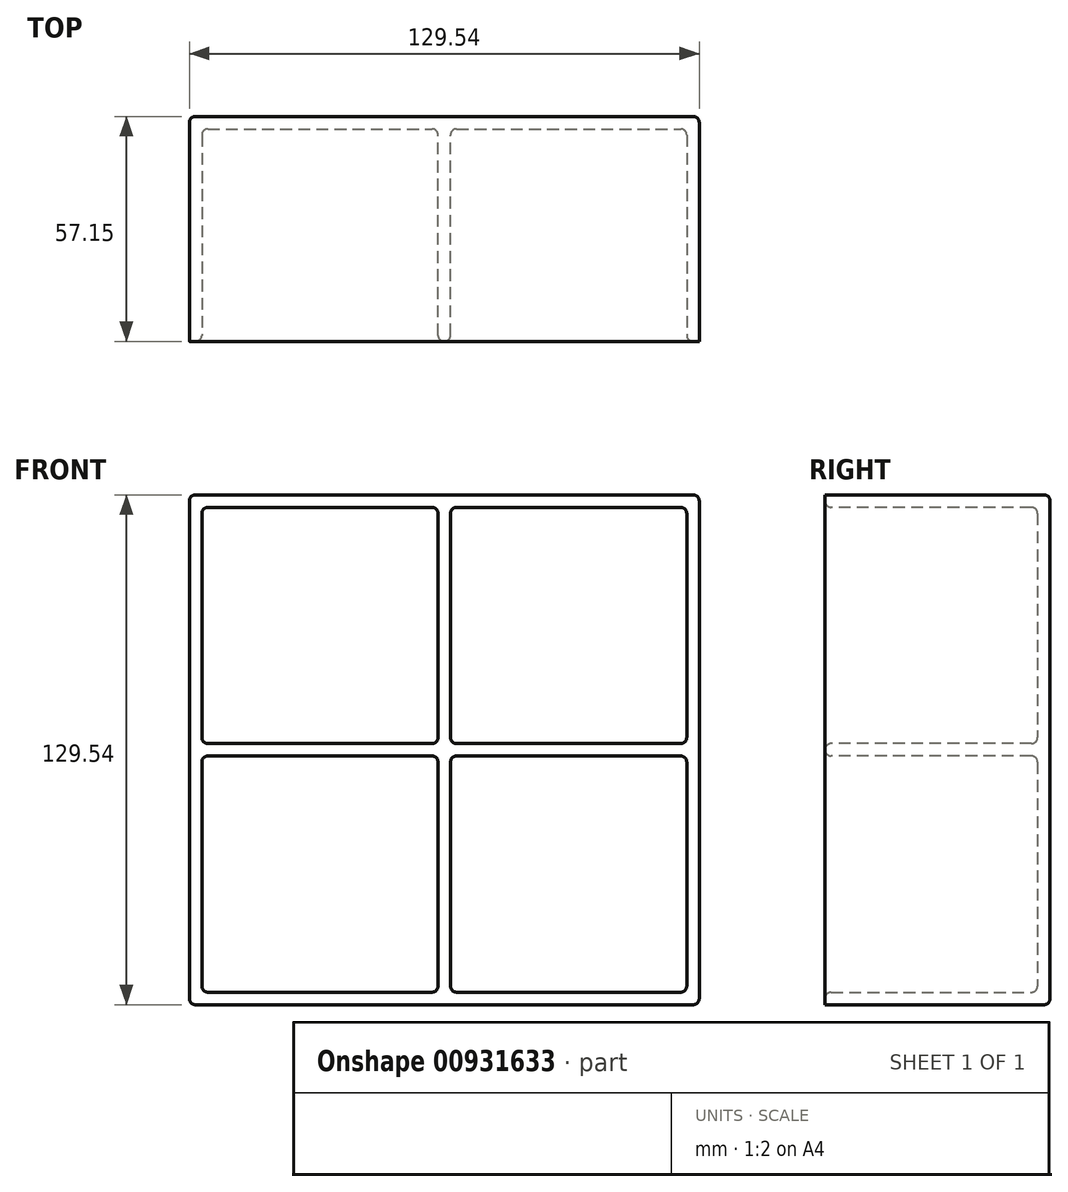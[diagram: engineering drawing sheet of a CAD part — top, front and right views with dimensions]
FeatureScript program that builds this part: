
annotation { "Feature Type Name" : "Feature", "Feature Type Description" : "" }
export const myFeature = defineFeature(function(context is Context, id is Id, definition is map)
    precondition{}
    {
        {
            var Q0;
            Q0=qCreatedBy(makeId("Front.planeOp"),FACE);
            var sketch = newSketch(context, id + "F0", { "sketchPlane" : qUnion([Q0])});
            skLineSegment(sketch, "E0.bottom", {"start": v(0, 0) * mm, "end": v(129.54, 0) * mm});
            skLineSegment(sketch, "E0.top", {"start": v(0, 129.54) * mm, "end": v(129.54, 129.54) * mm});
            skLineSegment(sketch, "E0.left", {"start": v(0, 0) * mm, "end": v(0, 129.54) * mm});
            skLineSegment(sketch, "E0.right", {"start": v(129.54, 0) * mm, "end": v(129.54, 129.54) * mm});
            skSolve(sketch);
        }
        {
            var Q0;
            Q0=makeQuery(id+"F0.imprint","IMPRINT",FACE,{"disambiguationData":[TD([[makeQuery(id+"F0.imprint","IMPRINT",EDGE,{"derivedFrom":sQuery(id+"F0.wireOp",EDGE,"E0.bottom")}),1.0]])]});
            extrude(context, id + "F1", {"entities" : qUnion([Q0]), "oppositeDirection" : true, "depth" : 57.15 * mm, "offsetDistance" : 25.4 * mm});
        }
        {
            var Q0;
            Q0=makeQuery(id+"F1.opExtrude","CAP_FACE",FACE,{"disambiguationData":[OSD([sQuery(id+"F0.wireOp",EDGE,"E0.bottom"),sQuery(id+"F0.wireOp",EDGE,"E0.top"),sQuery(id+"F0.wireOp",EDGE,"E0.left"),sQuery(id+"F0.wireOp",EDGE,"E0.right")])],"isStart":true});
            shell(context, id + "F2", {"entities" : qUnion([Q0]), "thickness" : 3.17 * mm});
        }
        {
            var Q0;
            Q0=makeQuery(id+"F2.opShell","OFFSET_EDGE",EDGE,{"disambiguationData":[OSD([sQuery(id+"F0.wireOp",EDGE,"E0.top"),sQuery(id+"F0.wireOp",EDGE,"E0.left")])]});
            var Q1;
            {var subQ0=sQuery(id+"F0.wireOp",EDGE,"E0.top");Q1=makeQuery(id+"F2.opShell","OFFSET_EDGE",EDGE,{"disambiguationData":[OSD([subQ0]),TDD([makeQuery(id+"F1.opExtrude","CAP_EDGE",EDGE,{"disambiguationData":[OSD([subQ0])],"isStart":false})])]});}
            var Q2;
            {var subQ0=sQuery(id+"F0.wireOp",EDGE,"E0.left");Q2=makeQuery(id+"F2.opShell","OFFSET_EDGE",EDGE,{"disambiguationData":[OSD([subQ0]),TDD([makeQuery(id+"F1.opExtrude","CAP_EDGE",EDGE,{"disambiguationData":[OSD([subQ0])],"isStart":false})])]});}
            var Q3;
            Q3=makeQuery(id+"F2.opShell","OFFSET_EDGE",EDGE,{"disambiguationData":[OSD([sQuery(id+"F0.wireOp",EDGE,"E0.bottom"),sQuery(id+"F0.wireOp",EDGE,"E0.left")])]});
            var Q4;
            {var subQ0=sQuery(id+"F0.wireOp",EDGE,"E0.bottom");Q4=makeQuery(id+"F2.opShell","OFFSET_EDGE",EDGE,{"disambiguationData":[OSD([subQ0]),TDD([makeQuery(id+"F1.opExtrude","CAP_EDGE",EDGE,{"disambiguationData":[OSD([subQ0])],"isStart":false})])]});}
            var Q5;
            {var subQ0=sQuery(id+"F0.wireOp",EDGE,"E0.right");Q5=makeQuery(id+"F2.opShell","OFFSET_EDGE",EDGE,{"disambiguationData":[OSD([subQ0]),TDD([makeQuery(id+"F1.opExtrude","CAP_EDGE",EDGE,{"disambiguationData":[OSD([subQ0])],"isStart":false})])]});}
            var Q6;
            Q6=makeQuery(id+"F2.opShell","OFFSET_EDGE",EDGE,{"disambiguationData":[OSD([sQuery(id+"F0.wireOp",EDGE,"E0.top"),sQuery(id+"F0.wireOp",EDGE,"E0.right")])]});
            var Q7;
            Q7=makeQuery(id+"F2.opShell","OFFSET_EDGE",EDGE,{"disambiguationData":[OSD([sQuery(id+"F0.wireOp",EDGE,"E0.bottom"),sQuery(id+"F0.wireOp",EDGE,"E0.right")])]});
            fillet(context, id + "F3", {"entities" : qUnion([Q0, Q1, Q2, Q3, Q4, Q5, Q6, Q7]), "radius" : 1.52 * mm, "tangentPropagation" : true, "allowEdgeOverflow" : false});
        }
        {
            var Q0;
            Q0=makeQuery(id+"F1.opExtrude","SWEPT_EDGE",EDGE,{"disambiguationData":[OSD([sQuery(id+"F0.wireOp",EDGE,"E0.bottom"),sQuery(id+"F0.wireOp",EDGE,"E0.right")])]});
            var Q1;
            Q1=makeQuery(id+"F1.opExtrude","CAP_EDGE",EDGE,{"disambiguationData":[OSD([sQuery(id+"F0.wireOp",EDGE,"E0.bottom")])],"isStart":false});
            var Q2;
            Q2=makeQuery(id+"F1.opExtrude","CAP_EDGE",EDGE,{"disambiguationData":[OSD([sQuery(id+"F0.wireOp",EDGE,"E0.right")])],"isStart":false});
            var Q3;
            Q3=makeQuery(id+"F1.opExtrude","SWEPT_EDGE",EDGE,{"disambiguationData":[OSD([sQuery(id+"F0.wireOp",EDGE,"E0.top"),sQuery(id+"F0.wireOp",EDGE,"E0.right")])]});
            var Q4;
            Q4=makeQuery(id+"F1.opExtrude","CAP_EDGE",EDGE,{"disambiguationData":[OSD([sQuery(id+"F0.wireOp",EDGE,"E0.top")])],"isStart":false});
            var Q5;
            Q5=makeQuery(id+"F1.opExtrude","SWEPT_EDGE",EDGE,{"disambiguationData":[OSD([sQuery(id+"F0.wireOp",EDGE,"E0.top"),sQuery(id+"F0.wireOp",EDGE,"E0.left")])]});
            var Q6;
            Q6=makeQuery(id+"F1.opExtrude","CAP_EDGE",EDGE,{"disambiguationData":[OSD([sQuery(id+"F0.wireOp",EDGE,"E0.left")])],"isStart":false});
            var Q7;
            Q7=makeQuery(id+"F1.opExtrude","SWEPT_EDGE",EDGE,{"disambiguationData":[OSD([sQuery(id+"F0.wireOp",EDGE,"E0.bottom"),sQuery(id+"F0.wireOp",EDGE,"E0.left")])]});
            fillet(context, id + "F4", {"entities" : qUnion([Q0, Q1, Q2, Q3, Q4, Q5, Q6, Q7]), "radius" : 1.52 * mm, "tangentPropagation" : true, "allowEdgeOverflow" : false});
        }
        {
            var Q0;
            Q0=makeQuery(id+"F2.opShell","OFFSET_FACE",FACE,{"disambiguationData":[OSD([sQuery(id+"F0.wireOp",EDGE,"E0.bottom"),sQuery(id+"F0.wireOp",EDGE,"E0.top"),sQuery(id+"F0.wireOp",EDGE,"E0.left"),sQuery(id+"F0.wireOp",EDGE,"E0.right")])]});
            var sketch = newSketch(context, id + "F5", { "sketchPlane" : qUnion([Q0])});
            skLineSegment(sketch, "E1.0", {"start": v(63.18, 126.37) * mm, "end": v(63.18, 3.17) * mm});
            skLineSegment(sketch, "E2.0", {"start": v(66.36, 126.37) * mm, "end": v(66.36, 3.17) * mm});
            skPoint(sketch, "E3.end.orphan", {"position": v(64.77, 3.17) * mm});
            skPoint(sketch, "E3.start.orphan", {"position": v(64.77, 126.37) * mm});
            skLineSegment(sketch, "E4", {"start": v(63.18, 126.37) * mm, "end": v(66.36, 126.37) * mm});
            skLineSegment(sketch, "E5", {"start": v(66.36, 3.17) * mm, "end": v(63.18, 3.17) * mm});
            skSolve(sketch);
        }
        {
            var Q0;
            Q0=makeQuery(id+"F5.imprint","IMPRINT",FACE,{"disambiguationData":[TD([[makeQuery(id+"F5.imprint","IMPRINT",EDGE,{"derivedFrom":sQuery(id+"F5.wireOp",EDGE,"E1.0")}),1.0]])]});
            extrude(context, id + "F6", {"entities" : qUnion([Q0]), "operationType" : NewBodyOperationType.ADD, "depth" : 53.97 * mm, "offsetDistance" : 25.4 * mm});
        }
        {
            var Q0;
            Q0=makeQuery(id+"F6.boolean.opBoolean","MERGE",FACE,{"derivedFrom":[makeQuery(id+"F1.opExtrude","CAP_FACE",FACE,{"disambiguationData":[OSD([sQuery(id+"F0.wireOp",EDGE,"E0.bottom"),sQuery(id+"F0.wireOp",EDGE,"E0.top"),sQuery(id+"F0.wireOp",EDGE,"E0.left"),sQuery(id+"F0.wireOp",EDGE,"E0.right")])],"isStart":true}),makeQuery(id+"F6.opExtrude","CAP_FACE",FACE,{"disambiguationData":[OSD([sQuery(id+"F5.wireOp",EDGE,"E1.0"),sQuery(id+"F5.wireOp",EDGE,"E2.0"),sQuery(id+"F5.wireOp",EDGE,"E4"),sQuery(id+"F5.wireOp",EDGE,"E5")])],"isStart":false})]});
            var sketch = newSketch(context, id + "F7", { "sketchPlane" : qUnion([Q0])});
            skLineSegment(sketch, "E6.0", {"start": v(3.17, 63.18) * mm, "end": v(126.37, 63.18) * mm});
            skLineSegment(sketch, "E7.0", {"start": v(3.17, 66.36) * mm, "end": v(126.37, 66.36) * mm});
            skPoint(sketch, "E8.end.orphan", {"position": v(126.37, 64.77) * mm});
            skPoint(sketch, "E8.start.orphan", {"position": v(3.17, 64.77) * mm});
            skLineSegment(sketch, "E9", {"start": v(3.17, 66.36) * mm, "end": v(3.17, 63.18) * mm});
            skLineSegment(sketch, "E10", {"start": v(126.37, 66.36) * mm, "end": v(126.37, 63.18) * mm});
            skSolve(sketch);
        }
        {
            var Q0;
            {var subQ0=sQuery(id+"F7.wireOp",EDGE,"E10");Q0=makeQuery(id+"F7.imprint","IMPRINT",FACE,{"disambiguationData":[TD([[makeQuery(id+"F7.imprint","IMPRINT",EDGE,{"derivedFrom":subQ0}),1.0]])]});}
            var Q1;
            {var subQ0=sQuery(id+"F7.wireOp",EDGE,"E9");Q1=makeQuery(id+"F7.imprint","IMPRINT",FACE,{"disambiguationData":[TD([[makeQuery(id+"F7.imprint","IMPRINT",EDGE,{"derivedFrom":subQ0}),-1.0]])]});}
            extrude(context, id + "F8", {"entities" : qUnion([Q0, Q1]), "operationType" : NewBodyOperationType.ADD, "oppositeDirection" : true, "depth" : 53.97 * mm, "offsetDistance" : 25.4 * mm});
        }
        {
            var Q0;
            {var subQ0=sQuery(id+"F0.wireOp",EDGE,"E0.top");var subQ4=sQuery(id+"F5.wireOp",EDGE,"E2.0");Q0=makeQuery(id+"F8.boolean.opBoolean","SPLIT",FACE,{"disambiguationData":[TD([makeQuery(id+"F2.opShell","OFFSET_FACE",FACE,{"disambiguationData":[OSD([subQ0])]})])],"derivedFrom":makeQuery(id+"F6.opExtrude","SWEPT_FACE",FACE,{"disambiguationData":[OSD([subQ4])]})});}
            var Q1;
            {var subQ0=sQuery(id+"F7.wireOp",EDGE,"E7.0");Q1=makeQuery(id+"F8.opExtrude","SWEPT_FACE",FACE,{"disambiguationData":[OSD([subQ0]),TDD([makeQuery(id+"F7.imprint","IMPRINT",EDGE,{"disambiguationData":[TD([[makeQuery(id+"F7.imprint","INTERSECT",VERTEX,{"derivedFrom":[makeQuery(id+"F6.opExtrude","CAP_EDGE",EDGE,{"disambiguationData":[OSD([sQuery(id+"F5.wireOp",EDGE,"E2.0")])],"isStart":false}),subQ0]}),-1.0]])],"derivedFrom":subQ0})])]});}
            var Q2;
            {var subQ0=sQuery(id+"F0.wireOp",EDGE,"E0.right");var subQ4=sQuery(id+"F0.wireOp",EDGE,"E0.top");Q2=makeQuery(id+"F8.boolean.opBoolean","SPLIT",FACE,{"disambiguationData":[TD([makeQuery(id+"F3.opFillet","BLEND_FACE",FACE,{"disambiguationData":[OSD([subQ4,subQ0]),TDD([makeQuery(id+"F2.opShell","OFFSET_EDGE",EDGE,{"disambiguationData":[OSD([subQ4,subQ0])]})])]})])],"derivedFrom":makeQuery(id+"F2.opShell","OFFSET_FACE",FACE,{"disambiguationData":[OSD([subQ0])]})});}
            var Q3;
            {var subQ0=sQuery(id+"F0.wireOp",EDGE,"E0.right");var subQ1=sQuery(id+"F0.wireOp",EDGE,"E0.bottom");Q3=makeQuery(id+"F8.boolean.opBoolean","SPLIT",FACE,{"disambiguationData":[TD([makeQuery(id+"F3.opFillet","BLEND_FACE",FACE,{"disambiguationData":[OSD([subQ1,subQ0]),TDD([makeQuery(id+"F2.opShell","OFFSET_EDGE",EDGE,{"disambiguationData":[OSD([subQ1,subQ0])]})])]})])],"derivedFrom":makeQuery(id+"F2.opShell","OFFSET_FACE",FACE,{"disambiguationData":[OSD([subQ0])]})});}
            var Q4;
            {var subQ0=sQuery(id+"F7.wireOp",EDGE,"E6.0");Q4=makeQuery(id+"F8.opExtrude","SWEPT_FACE",FACE,{"disambiguationData":[OSD([subQ0]),TDD([makeQuery(id+"F7.imprint","IMPRINT",EDGE,{"disambiguationData":[TD([[makeQuery(id+"F7.imprint","INTERSECT",VERTEX,{"derivedFrom":[makeQuery(id+"F6.opExtrude","CAP_EDGE",EDGE,{"disambiguationData":[OSD([sQuery(id+"F5.wireOp",EDGE,"E2.0")])],"isStart":false}),subQ0]}),-1.0]])],"derivedFrom":subQ0})])]});}
            var Q5;
            {var subQ0=sQuery(id+"F0.wireOp",EDGE,"E0.bottom");var subQ4=sQuery(id+"F5.wireOp",EDGE,"E2.0");Q5=makeQuery(id+"F8.boolean.opBoolean","SPLIT",FACE,{"disambiguationData":[TD([makeQuery(id+"F2.opShell","OFFSET_FACE",FACE,{"disambiguationData":[OSD([subQ0])]})])],"derivedFrom":makeQuery(id+"F6.opExtrude","SWEPT_FACE",FACE,{"disambiguationData":[OSD([subQ4])]})});}
            var Q6;
            {var subQ0=sQuery(id+"F0.wireOp",EDGE,"E0.bottom");var subQ1=sQuery(id+"F5.wireOp",EDGE,"E2.0");Q6=makeQuery(id+"F6.boolean.opBoolean","SPLIT",FACE,{"disambiguationData":[TD([makeQuery(id+"F6.opExtrude","SWEPT_FACE",FACE,{"disambiguationData":[OSD([subQ1])]})])],"derivedFrom":makeQuery(id+"F2.opShell","OFFSET_FACE",FACE,{"disambiguationData":[OSD([subQ0])]})});}
            var Q7;
            {var subQ0=sQuery(id+"F0.wireOp",EDGE,"E0.bottom");var subQ2=sQuery(id+"F5.wireOp",EDGE,"E1.0");Q7=makeQuery(id+"F6.boolean.opBoolean","SPLIT",FACE,{"disambiguationData":[TD([makeQuery(id+"F6.opExtrude","SWEPT_FACE",FACE,{"disambiguationData":[OSD([subQ2])]})])],"derivedFrom":makeQuery(id+"F2.opShell","OFFSET_FACE",FACE,{"disambiguationData":[OSD([subQ0])]})});}
            var Q8;
            {var subQ0=sQuery(id+"F0.wireOp",EDGE,"E0.left");var subQ4=sQuery(id+"F0.wireOp",EDGE,"E0.bottom");Q8=makeQuery(id+"F8.boolean.opBoolean","SPLIT",FACE,{"disambiguationData":[TD([makeQuery(id+"F3.opFillet","BLEND_FACE",FACE,{"disambiguationData":[OSD([subQ4,subQ0]),TDD([makeQuery(id+"F2.opShell","OFFSET_EDGE",EDGE,{"disambiguationData":[OSD([subQ4,subQ0])]})])]})])],"derivedFrom":makeQuery(id+"F2.opShell","OFFSET_FACE",FACE,{"disambiguationData":[OSD([subQ0])]})});}
            var Q9;
            {var subQ0=sQuery(id+"F7.wireOp",EDGE,"E6.0");Q9=makeQuery(id+"F8.opExtrude","SWEPT_FACE",FACE,{"disambiguationData":[OSD([subQ0]),TDD([makeQuery(id+"F7.imprint","IMPRINT",EDGE,{"disambiguationData":[TD([[makeQuery(id+"F7.imprint","INTERSECT",VERTEX,{"derivedFrom":[makeQuery(id+"F6.opExtrude","CAP_EDGE",EDGE,{"disambiguationData":[OSD([sQuery(id+"F5.wireOp",EDGE,"E1.0")])],"isStart":false}),subQ0]}),1.0]])],"derivedFrom":subQ0})])]});}
            var Q10;
            {var subQ0=sQuery(id+"F0.wireOp",EDGE,"E0.bottom");var subQ5=sQuery(id+"F5.wireOp",EDGE,"E1.0");Q10=makeQuery(id+"F8.boolean.opBoolean","SPLIT",FACE,{"disambiguationData":[TD([makeQuery(id+"F2.opShell","OFFSET_FACE",FACE,{"disambiguationData":[OSD([subQ0])]})])],"derivedFrom":makeQuery(id+"F6.opExtrude","SWEPT_FACE",FACE,{"disambiguationData":[OSD([subQ5])]})});}
            var Q11;
            {var subQ1=sQuery(id+"F0.wireOp",EDGE,"E0.top");var subQ2=sQuery(id+"F5.wireOp",EDGE,"E2.0");Q11=makeQuery(id+"F6.boolean.opBoolean","SPLIT",FACE,{"disambiguationData":[TD([makeQuery(id+"F6.opExtrude","SWEPT_FACE",FACE,{"disambiguationData":[OSD([subQ2])]})])],"derivedFrom":makeQuery(id+"F2.opShell","OFFSET_FACE",FACE,{"disambiguationData":[OSD([subQ1])]})});}
            var Q12;
            {var subQ1=sQuery(id+"F0.wireOp",EDGE,"E0.top");var subQ2=sQuery(id+"F5.wireOp",EDGE,"E1.0");Q12=makeQuery(id+"F6.boolean.opBoolean","SPLIT",FACE,{"disambiguationData":[TD([makeQuery(id+"F6.opExtrude","SWEPT_FACE",FACE,{"disambiguationData":[OSD([subQ2])]})])],"derivedFrom":makeQuery(id+"F2.opShell","OFFSET_FACE",FACE,{"disambiguationData":[OSD([subQ1])]})});}
            var Q13;
            {var subQ0=sQuery(id+"F0.wireOp",EDGE,"E0.top");var subQ5=sQuery(id+"F5.wireOp",EDGE,"E1.0");Q13=makeQuery(id+"F8.boolean.opBoolean","SPLIT",FACE,{"disambiguationData":[TD([makeQuery(id+"F2.opShell","OFFSET_FACE",FACE,{"disambiguationData":[OSD([subQ0])]})])],"derivedFrom":makeQuery(id+"F6.opExtrude","SWEPT_FACE",FACE,{"disambiguationData":[OSD([subQ5])]})});}
            var Q14;
            {var subQ0=sQuery(id+"F7.wireOp",EDGE,"E7.0");Q14=makeQuery(id+"F8.opExtrude","SWEPT_FACE",FACE,{"disambiguationData":[OSD([subQ0]),TDD([makeQuery(id+"F7.imprint","IMPRINT",EDGE,{"disambiguationData":[TD([[makeQuery(id+"F7.imprint","INTERSECT",VERTEX,{"derivedFrom":[makeQuery(id+"F6.opExtrude","CAP_EDGE",EDGE,{"disambiguationData":[OSD([sQuery(id+"F5.wireOp",EDGE,"E1.0")])],"isStart":false}),subQ0]}),1.0]])],"derivedFrom":subQ0})])]});}
            var Q15;
            {var subQ0=sQuery(id+"F0.wireOp",EDGE,"E0.left");var subQ1=sQuery(id+"F0.wireOp",EDGE,"E0.top");Q15=makeQuery(id+"F8.boolean.opBoolean","SPLIT",FACE,{"disambiguationData":[TD([makeQuery(id+"F3.opFillet","BLEND_FACE",FACE,{"disambiguationData":[OSD([subQ1,subQ0]),TDD([makeQuery(id+"F2.opShell","OFFSET_EDGE",EDGE,{"disambiguationData":[OSD([subQ1,subQ0])]})])]})])],"derivedFrom":makeQuery(id+"F2.opShell","OFFSET_FACE",FACE,{"disambiguationData":[OSD([subQ0])]})});}
            fillet(context, id + "F9", {"entities" : qUnion([Q0, Q1, Q2, Q3, Q4, Q5, Q6, Q7, Q8, Q9, Q10, Q11, Q12, Q13, Q14, Q15]), "radius" : 1.52 * mm, "tangentPropagation" : true, "allowEdgeOverflow" : false});
        }
    });
